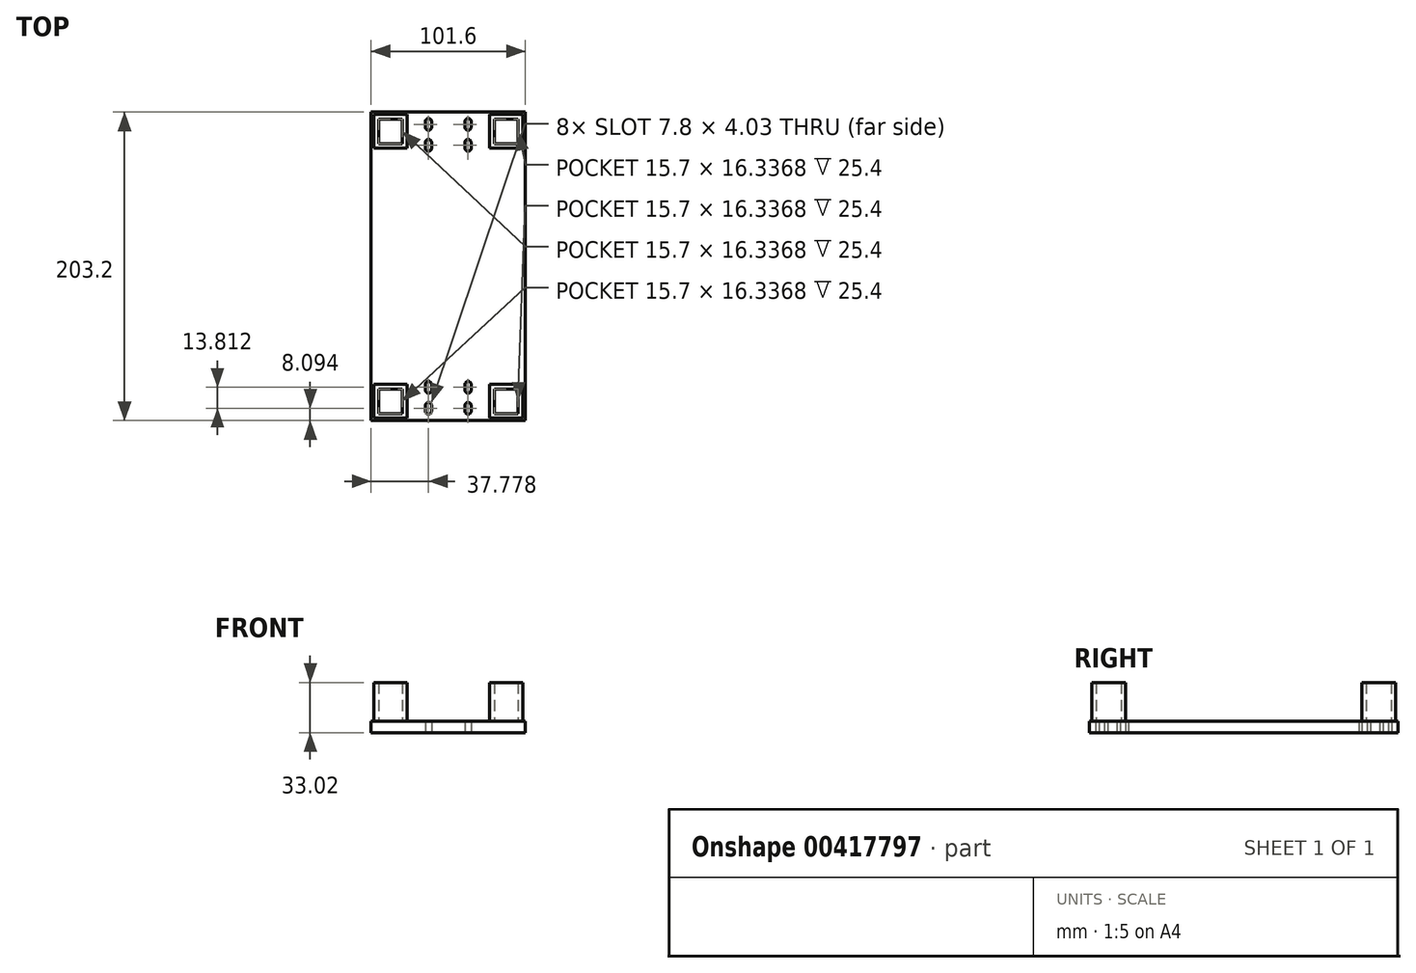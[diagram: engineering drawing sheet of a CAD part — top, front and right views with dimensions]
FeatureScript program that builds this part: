
annotation { "Feature Type Name" : "Feature", "Feature Type Description" : "" }
export const myFeature = defineFeature(function(context is Context, id is Id, definition is map)
    precondition{}
    {
        {
            var Q0;
            Q0=qCreatedBy(makeId("Top.planeOp"),FACE);
            var sketch = newSketch(context, id + "F0", { "sketchPlane" : qUnion([Q0])});
            skLineSegment(sketch, "E0.bottom", {"start": v(-50.8, 101.6) * mm, "end": v(50.8, 101.6) * mm});
            skLineSegment(sketch, "E0.top", {"start": v(-50.8, -101.6) * mm, "end": v(50.8, -101.6) * mm});
            skLineSegment(sketch, "E0.left", {"start": v(-50.8, 101.6) * mm, "end": v(-50.8, -101.6) * mm});
            skLineSegment(sketch, "E0.right", {"start": v(50.8, 101.6) * mm, "end": v(50.8, -101.6) * mm});
            skPoint(sketch, "E0.middle", {"position": v(0, 0) * mm});
            skSolve(sketch);
        }
        {
            var Q0;
            Q0=qSketchRegion(id+"F0",true);
            extrude(context, id + "F1", {"entities" : qUnion([Q0]), "depth" : 7.62 * mm});
        }
        {
            var Q0;
            Q0=qCreatedBy(makeId("Top.planeOp"),FACE);
            var sketch = newSketch(context, id + "F2", { "sketchPlane" : qUnion([Q0])});
            skLineSegment(sketch, "E1.top", {"start": v(-19, -101.6) * mm, "end": v(19, -101.6) * mm});
            skArc(sketch, "E2", {"start": v(-14.99, -81.42) * mm, "mid": v(-13.08, -83.6) * mm, "end": v(-11, -81.58) * mm});
            skArc(sketch, "E3", {"start": v(-11.05, -77.84) * mm, "mid": v(-13.03, -75.8) * mm, "end": v(-15.04, -77.82) * mm});
            skLineSegment(sketch, "E4", {"start": v(-11.05, -77.84) * mm, "end": v(-11, -81.58) * mm});
            skLineSegment(sketch, "E5", {"start": v(-15.04, -77.82) * mm, "end": v(-14.99, -81.42) * mm});
            skLineSegment(sketch, "E6.MirrorCS", {"start": v(-11.05, -95.36) * mm, "end": v(-11, -91.62) * mm});
            skLineSegment(sketch, "E7.MirrorCS", {"start": v(-15.04, -95.38) * mm, "end": v(-14.99, -91.78) * mm});
            skArc(sketch, "E8.MirrorCS", {"start": v(-14.99, -91.78) * mm, "mid": v(-13.08, -89.6) * mm, "end": v(-11, -91.62) * mm});
            skArc(sketch, "E9.MirrorCS", {"start": v(-11.05, -95.36) * mm, "mid": v(-13.03, -97.4) * mm, "end": v(-15.04, -95.38) * mm});
            skLineSegment(sketch, "E10.MirrorCS", {"start": v(11.05, -77.84) * mm, "end": v(11, -81.58) * mm});
            skLineSegment(sketch, "E11.MirrorCS", {"start": v(15.04, -77.82) * mm, "end": v(14.99, -81.42) * mm});
            skArc(sketch, "E12.MirrorCS", {"start": v(14.99, -81.42) * mm, "mid": v(13.08, -83.6) * mm, "end": v(11, -81.58) * mm});
            skArc(sketch, "E13.MirrorCS", {"start": v(11.05, -77.84) * mm, "mid": v(13.03, -75.8) * mm, "end": v(15.04, -77.82) * mm});
            skArc(sketch, "E14.MirrorCS", {"start": v(11.05, -95.36) * mm, "mid": v(13.03, -97.4) * mm, "end": v(15.04, -95.38) * mm});
            skLineSegment(sketch, "E15.MirrorCS", {"start": v(11.05, -95.36) * mm, "end": v(11, -91.62) * mm});
            skArc(sketch, "E16.MirrorCS", {"start": v(14.99, -91.78) * mm, "mid": v(13.08, -89.6) * mm, "end": v(11, -91.62) * mm});
            skLineSegment(sketch, "E17", {"start": v(14.99, -91.78) * mm, "end": v(15.04, -95.38) * mm});
            skLineSegment(sketch, "E18.MirrorCS", {"start": v(11.05, 95.36) * mm, "end": v(11, 91.62) * mm});
            skArc(sketch, "E19.MirrorCS", {"start": v(-11.05, 95.36) * mm, "mid": v(-13.03, 97.4) * mm, "end": v(-15.04, 95.38) * mm});
            skLineSegment(sketch, "E20.MirrorCS", {"start": v(-11.05, 77.84) * mm, "end": v(-11, 81.58) * mm});
            skLineSegment(sketch, "E21.MirrorCS", {"start": v(15.04, 77.82) * mm, "end": v(14.99, 81.42) * mm});
            skLineSegment(sketch, "E22.MirrorCS", {"start": v(11.05, 77.84) * mm, "end": v(11, 81.58) * mm});
            skArc(sketch, "E23.MirrorCS", {"start": v(11.05, 77.84) * mm, "mid": v(13.03, 75.8) * mm, "end": v(15.04, 77.82) * mm});
            skArc(sketch, "E24.MirrorCS", {"start": v(-14.99, 81.42) * mm, "mid": v(-13.08, 83.6) * mm, "end": v(-11, 81.58) * mm});
            skArc(sketch, "E25.MirrorCS", {"start": v(-11.05, 77.84) * mm, "mid": v(-13.03, 75.8) * mm, "end": v(-15.04, 77.82) * mm});
            skArc(sketch, "E26.MirrorCS", {"start": v(14.99, 91.78) * mm, "mid": v(13.08, 89.6) * mm, "end": v(11, 91.62) * mm});
            skLineSegment(sketch, "E27.MirrorCS", {"start": v(-15.04, 95.38) * mm, "end": v(-14.99, 91.78) * mm});
            skArc(sketch, "E28.MirrorCS", {"start": v(11.05, 95.36) * mm, "mid": v(13.03, 97.4) * mm, "end": v(15.04, 95.38) * mm});
            skLineSegment(sketch, "E29.MirrorCS", {"start": v(-15.04, 77.82) * mm, "end": v(-14.99, 81.42) * mm});
            skArc(sketch, "E30.MirrorCS", {"start": v(-14.99, 91.78) * mm, "mid": v(-13.08, 89.6) * mm, "end": v(-11, 91.62) * mm});
            skLineSegment(sketch, "E31.MirrorCS", {"start": v(14.99, 91.78) * mm, "end": v(15.04, 95.38) * mm});
            skLineSegment(sketch, "E32.MirrorCS", {"start": v(-11.05, 95.36) * mm, "end": v(-11, 91.62) * mm});
            skArc(sketch, "E33.MirrorCS", {"start": v(14.99, 81.42) * mm, "mid": v(13.08, 83.6) * mm, "end": v(11, 81.58) * mm});
            skSolve(sketch);
        }
        {
            var Q0;
            Q0=qSketchRegion(id+"F2",true);
            extrude(context, id + "F3", {"entities" : qUnion([Q0]), "operationType" : NewBodyOperationType.REMOVE, "oppositeDirection" : true, "depth" : -25.4 * mm});
        }
        {
            var Q0;
            Q0=makeQuery(id+"F1.opExtrude","CAP_FACE",FACE,{"disambiguationData":[OSD([sQuery(id+"F0.wireOp",EDGE,"E0.bottom"),sQuery(id+"F0.wireOp",EDGE,"E0.top"),sQuery(id+"F0.wireOp",EDGE,"E0.left"),sQuery(id+"F0.wireOp",EDGE,"E0.right")])],"isStart":false});
            var sketch = newSketch(context, id + "F4", { "sketchPlane" : qUnion([Q0])});
            skLineSegment(sketch, "E34.bottom", {"start": v(30.25, 97.07) * mm, "end": v(45.95, 97.07) * mm});
            skLineSegment(sketch, "E34.top", {"start": v(30.25, 80.73) * mm, "end": v(45.95, 80.73) * mm});
            skLineSegment(sketch, "E34.left", {"start": v(30.25, 97.07) * mm, "end": v(30.25, 80.73) * mm});
            skLineSegment(sketch, "E34.right", {"start": v(45.95, 97.07) * mm, "end": v(45.95, 80.73) * mm});
            skLineSegment(sketch, "E35.bottom", {"start": v(27.25, 100.07) * mm, "end": v(48.95, 100.07) * mm});
            skLineSegment(sketch, "E35.top", {"start": v(27.25, 77.73) * mm, "end": v(48.95, 77.73) * mm});
            skLineSegment(sketch, "E35.left", {"start": v(27.25, 100.07) * mm, "end": v(27.25, 77.73) * mm});
            skLineSegment(sketch, "E35.right", {"start": v(48.95, 100.07) * mm, "end": v(48.95, 77.73) * mm});
            skLineSegment(sketch, "E36.MirrorCS", {"start": v(27.25, -100.07) * mm, "end": v(48.95, -100.07) * mm});
            skLineSegment(sketch, "E37.MirrorCS", {"start": v(45.95, -97.07) * mm, "end": v(45.95, -80.73) * mm});
            skLineSegment(sketch, "E38.MirrorCS", {"start": v(30.25, -97.07) * mm, "end": v(30.25, -80.73) * mm});
            skLineSegment(sketch, "E39.MirrorCS", {"start": v(30.25, -80.73) * mm, "end": v(45.95, -80.73) * mm});
            skLineSegment(sketch, "E40.MirrorCS", {"start": v(30.25, -97.07) * mm, "end": v(45.95, -97.07) * mm});
            skLineSegment(sketch, "E41.MirrorCS", {"start": v(27.25, -77.73) * mm, "end": v(48.95, -77.73) * mm});
            skLineSegment(sketch, "E42.MirrorCS", {"start": v(27.25, -100.07) * mm, "end": v(27.25, -77.73) * mm});
            skLineSegment(sketch, "E43.MirrorCS", {"start": v(48.95, -100.07) * mm, "end": v(48.95, -77.73) * mm});
            skLineSegment(sketch, "E44.MirrorCS", {"start": v(-27.25, 100.07) * mm, "end": v(-48.95, 100.07) * mm});
            skLineSegment(sketch, "E45.MirrorCS", {"start": v(-30.25, 97.07) * mm, "end": v(-30.25, 80.73) * mm});
            skLineSegment(sketch, "E46.MirrorCS", {"start": v(-30.25, 97.07) * mm, "end": v(-45.95, 97.07) * mm});
            skLineSegment(sketch, "E47.MirrorCS", {"start": v(-27.25, 100.07) * mm, "end": v(-27.25, 77.73) * mm});
            skLineSegment(sketch, "E48.MirrorCS", {"start": v(-30.25, -97.07) * mm, "end": v(-30.25, -80.73) * mm});
            skLineSegment(sketch, "E49.MirrorCS", {"start": v(-27.25, 77.73) * mm, "end": v(-48.95, 77.73) * mm});
            skLineSegment(sketch, "E50.MirrorCS", {"start": v(-45.95, 97.07) * mm, "end": v(-45.95, 80.73) * mm});
            skLineSegment(sketch, "E51.MirrorCS", {"start": v(-30.25, 80.73) * mm, "end": v(-45.95, 80.73) * mm});
            skLineSegment(sketch, "E52.MirrorCS", {"start": v(-30.25, -80.73) * mm, "end": v(-45.95, -80.73) * mm});
            skLineSegment(sketch, "E53.MirrorCS", {"start": v(-27.25, -77.73) * mm, "end": v(-48.95, -77.73) * mm});
            skLineSegment(sketch, "E54.MirrorCS", {"start": v(-27.25, -100.07) * mm, "end": v(-48.95, -100.07) * mm});
            skLineSegment(sketch, "E55.MirrorCS", {"start": v(-30.25, -97.07) * mm, "end": v(-45.95, -97.07) * mm});
            skLineSegment(sketch, "E56.MirrorCS", {"start": v(-27.25, -100.07) * mm, "end": v(-27.25, -77.73) * mm});
            skLineSegment(sketch, "E57.MirrorCS", {"start": v(-48.95, 100.07) * mm, "end": v(-48.95, 77.73) * mm});
            skLineSegment(sketch, "E58.MirrorCS", {"start": v(-45.95, -97.07) * mm, "end": v(-45.95, -80.73) * mm});
            skLineSegment(sketch, "E59.MirrorCS", {"start": v(-48.95, -100.07) * mm, "end": v(-48.95, -77.73) * mm});
            skSolve(sketch);
        }
        {
            var Q0;
            Q0 = qSketchRegion(id + "F4", true);
            extrude(context, id + "F5", {"entities" : qUnion([Q0]), "operationType" : NewBodyOperationType.ADD, "depth" : 25.4 * mm});
        }
    });
